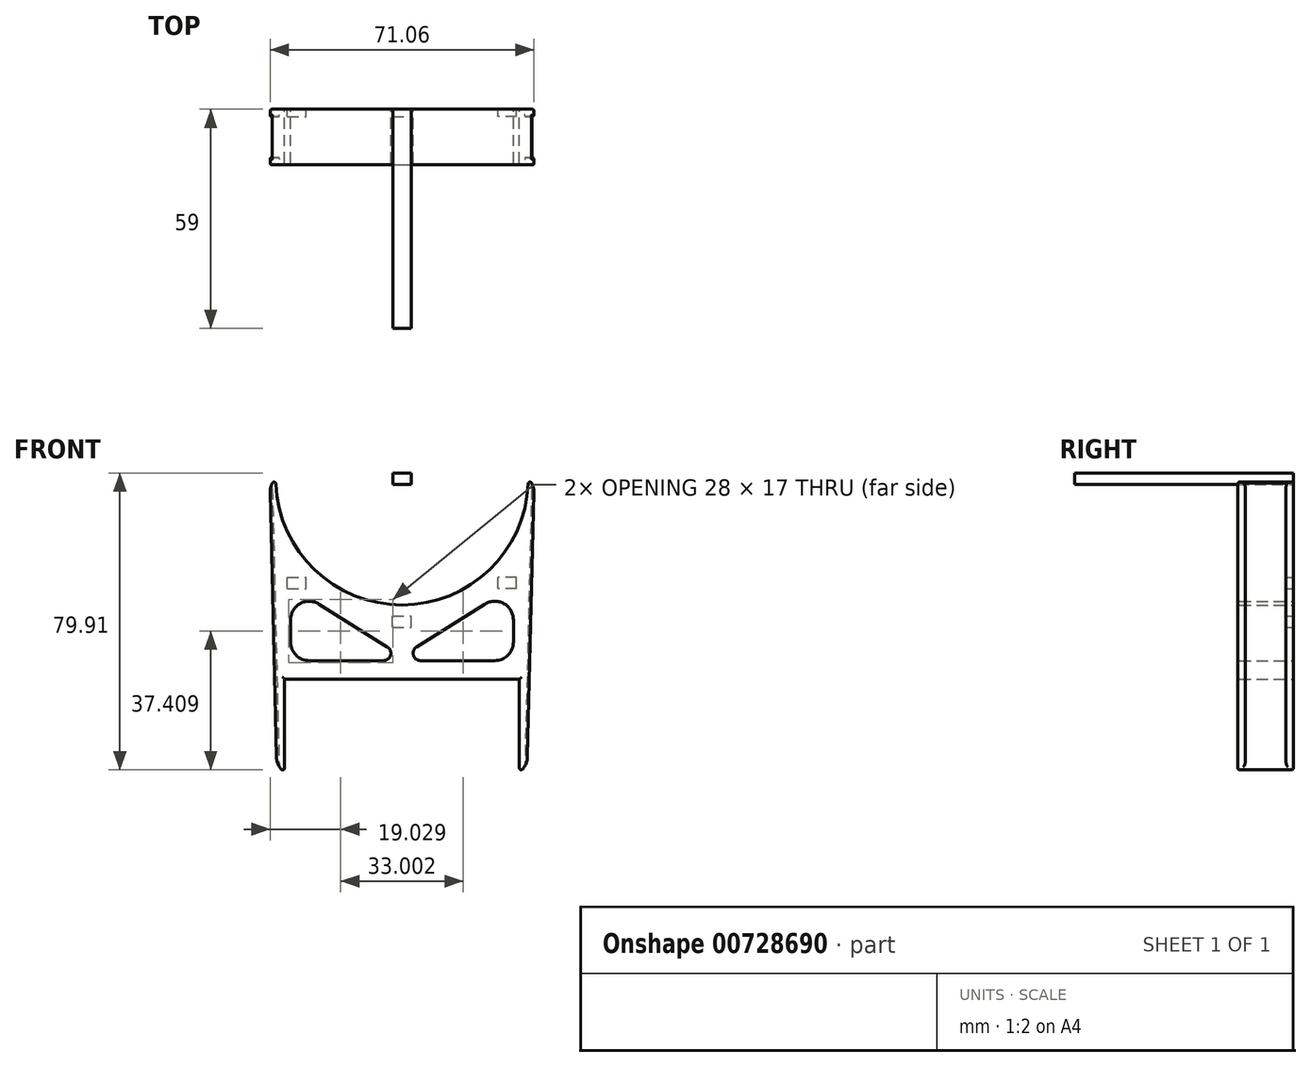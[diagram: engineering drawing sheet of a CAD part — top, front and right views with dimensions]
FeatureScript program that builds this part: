
annotation { "Feature Type Name" : "Feature", "Feature Type Description" : "" }
export const myFeature = defineFeature(function(context is Context, id is Id, definition is map)
    precondition{}
    {
        {
            var Q0;
            Q0=qCreatedBy(makeId("Front.planeOp"),FACE);
            var sketch = newSketch(context, id + "F0", { "sketchPlane" : qUnion([Q0])});
            skArc(sketch, "E0", {"start": v(-34, 0) * mm, "mid": v(0, -34) * mm, "end": v(34, 0) * mm});
            skLineSegment(sketch, "E1", {"start": v(-31.62, -54) * mm, "end": v(31.63, -54) * mm});
            skLineSegment(sketch, "E2", {"start": v(31.63, -54) * mm, "end": v(31.63, -79) * mm});
            skLineSegment(sketch, "E3", {"start": v(33.8, -75) * mm, "end": v(35.53, -3.72) * mm});
            skArc(sketch, "E4", {"start": v(33.8, -75) * mm, "mid": v(33.2, -77.26) * mm, "end": v(31.63, -79) * mm});
            skArc(sketch, "E5.MirrorCS", {"start": v(-33.8, -75) * mm, "mid": v(-33.2, -77.26) * mm, "end": v(-31.63, -79) * mm});
            skLineSegment(sketch, "E6", {"start": v(-31.62, -54) * mm, "end": v(-31.63, -79) * mm});
            skLineSegment(sketch, "E7", {"start": v(-30, -44) * mm, "end": v(-30, -38) * mm});
            skLineSegment(sketch, "E8", {"start": v(-25, -49) * mm, "end": v(-5, -49) * mm});
            skLineSegment(sketch, "E9", {"start": v(-3.94, -45.3) * mm, "end": v(-22.34, -33.76) * mm});
            skPoint(sketch, "E10.visualSharp", {"position": v(-30, -28.96) * mm});
            skArc(sketch, "E10.filletArc", {"start": v(-22.34, -33.76) * mm, "mid": v(-27.42, -33.63) * mm, "end": v(-30, -38) * mm});
            skPoint(sketch, "E11.visualSharp", {"position": v(1.95, -49) * mm});
            skArc(sketch, "E11.filletArc", {"start": v(-5, -49) * mm, "mid": v(-3.08, -47.55) * mm, "end": v(-3.94, -45.3) * mm});
            skPoint(sketch, "E12.visualSharp", {"position": v(-30, -49) * mm});
            skArc(sketch, "E12.filletArc", {"start": v(-30, -44) * mm, "mid": v(-28.54, -47.54) * mm, "end": v(-25, -49) * mm});
            skArc(sketch, "E13.MirrorCS", {"start": v(22.34, -33.76) * mm, "mid": v(27.42, -33.63) * mm, "end": v(30, -38) * mm});
            skLineSegment(sketch, "E14.MirrorCS", {"start": v(3.94, -45.3) * mm, "end": v(22.34, -33.76) * mm});
            skLineSegment(sketch, "E15.MirrorCS", {"start": v(25, -49) * mm, "end": v(5, -49) * mm});
            skArc(sketch, "E16.MirrorCS", {"start": v(30, -44) * mm, "mid": v(28.54, -47.54) * mm, "end": v(25, -49) * mm});
            skLineSegment(sketch, "E17.MirrorCS", {"start": v(30, -44) * mm, "end": v(30, -38) * mm});
            skArc(sketch, "E18.MirrorCS", {"start": v(5, -49) * mm, "mid": v(3.08, -47.55) * mm, "end": v(3.94, -45.3) * mm});
            skArc(sketch, "E19", {"start": v(35.53, -3.72) * mm, "mid": v(35.16, -1.7) * mm, "end": v(34, 0) * mm});
            skArc(sketch, "E20.MirrorCS", {"start": v(-35.53, -3.72) * mm, "mid": v(-35.16, -1.7) * mm, "end": v(-34, 0) * mm});
            skLineSegment(sketch, "E21.MirrorCS", {"start": v(-33.8, -75) * mm, "end": v(-35.53, -3.72) * mm});
            skSolve(sketch);
        }
        {
            var Q0;
            Q0 = qSketchRegion(id + "F0", true);
            extrude(context, id + "F1", {"entities" : qUnion([Q0]), "depth" : 15 * mm, "offsetDistance" : 25 * mm});
        }
        {
            var Q0;
            Q0=qCreatedBy(makeId("Front.planeOp"),FACE);
            cPlane(context, id + "F2", {"entities" : qUnion([Q0]), "cplaneType" : CPlaneType.OFFSET, "offset" : 2 * mm, "width" : 150 * mm, "height" : 150 * mm});
        }
        {
            var Q0;
            Q0=qCreatedBy(id+"F2.planeOp",FACE);
            var sketch = newSketch(context, id + "F3", { "sketchPlane" : qUnion([Q0])});
            skLineSegment(sketch, "E22.0", {"start": v(33.8, -75) * mm, "end": v(33.8, -75) * mm});
            skArc(sketch, "E23.0", {"start": v(33.8, -75) * mm, "mid": v(33.6, -76.25) * mm, "end": v(33.1, -77.4) * mm});
            skLineSegment(sketch, "E24.MirrorCS", {"start": v(-33.8, -75) * mm, "end": v(-33.8, -75) * mm});
            skLineSegment(sketch, "E25.0", {"start": v(33.8, -75) * mm, "end": v(35.53, -3.72) * mm});
            skArc(sketch, "E26.0", {"start": v(35.53, -3.72) * mm, "mid": v(35.4, -2.47) * mm, "end": v(34.96, -1.28) * mm});
            skLineSegment(sketch, "E27", {"start": v(34.96, -1.28) * mm, "end": v(33.1, -77.4) * mm});
            skPoint(sketch, "E28.orphan", {"position": v(34, 0) * mm});
            skLineSegment(sketch, "E29.MirrorCS", {"start": v(-34.96, -1.28) * mm, "end": v(-33.1, -77.4) * mm});
            skArc(sketch, "E30.MirrorCS", {"start": v(-35.53, -3.72) * mm, "mid": v(-35.4, -2.47) * mm, "end": v(-34.96, -1.28) * mm});
            skLineSegment(sketch, "E31.MirrorCS", {"start": v(-33.8, -75) * mm, "end": v(-35.53, -3.72) * mm});
            skArc(sketch, "E32.MirrorCS", {"start": v(-33.8, -75) * mm, "mid": v(-33.6, -76.25) * mm, "end": v(-33.1, -77.4) * mm});
            skSolve(sketch);
        }
        {
            var Q0;
            Q0 = qSketchRegion(id + "F3", true);
            extrude(context, id + "F4", {"entities" : qUnion([Q0]), "operationType" : NewBodyOperationType.REMOVE, "depth" : 11 * mm, "offsetDistance" : 25 * mm});
        }
        {
            var Q0;
            Q0=makeQuery(id+"F1.opExtrude","CAP_FACE",FACE,{"disambiguationData":[OSD([sQuery(id+"F0.wireOp",EDGE,"E0"),sQuery(id+"F0.wireOp",EDGE,"E1"),sQuery(id+"F0.wireOp",EDGE,"E2"),sQuery(id+"F0.wireOp",EDGE,"E3"),sQuery(id+"F0.wireOp",EDGE,"E4"),sQuery(id+"F0.wireOp",EDGE,"E5.MirrorCS"),sQuery(id+"F0.wireOp",EDGE,"E6"),sQuery(id+"F0.wireOp",EDGE,"E7"),sQuery(id+"F0.wireOp",EDGE,"E8"),sQuery(id+"F0.wireOp",EDGE,"E9"),sQuery(id+"F0.wireOp",EDGE,"E10.filletArc"),sQuery(id+"F0.wireOp",EDGE,"E11.filletArc"),sQuery(id+"F0.wireOp",EDGE,"E12.filletArc"),sQuery(id+"F0.wireOp",EDGE,"E13.MirrorCS"),sQuery(id+"F0.wireOp",EDGE,"E14.MirrorCS"),sQuery(id+"F0.wireOp",EDGE,"E15.MirrorCS"),sQuery(id+"F0.wireOp",EDGE,"E16.MirrorCS"),sQuery(id+"F0.wireOp",EDGE,"E17.MirrorCS"),sQuery(id+"F0.wireOp",EDGE,"E18.MirrorCS"),sQuery(id+"F0.wireOp",EDGE,"E19"),sQuery(id+"F0.wireOp",EDGE,"E20.MirrorCS"),sQuery(id+"F0.wireOp",EDGE,"E21.MirrorCS")])],"isStart":false});
            var Q1;
            Q1=makeQuery(id+"F1.opExtrude","CAP_FACE",FACE,{"disambiguationData":[OSD([sQuery(id+"F0.wireOp",EDGE,"E0"),sQuery(id+"F0.wireOp",EDGE,"E1"),sQuery(id+"F0.wireOp",EDGE,"E2"),sQuery(id+"F0.wireOp",EDGE,"E3"),sQuery(id+"F0.wireOp",EDGE,"E4"),sQuery(id+"F0.wireOp",EDGE,"E5.MirrorCS"),sQuery(id+"F0.wireOp",EDGE,"E6"),sQuery(id+"F0.wireOp",EDGE,"E7"),sQuery(id+"F0.wireOp",EDGE,"E8"),sQuery(id+"F0.wireOp",EDGE,"E9"),sQuery(id+"F0.wireOp",EDGE,"E10.filletArc"),sQuery(id+"F0.wireOp",EDGE,"E11.filletArc"),sQuery(id+"F0.wireOp",EDGE,"E12.filletArc"),sQuery(id+"F0.wireOp",EDGE,"E13.MirrorCS"),sQuery(id+"F0.wireOp",EDGE,"E14.MirrorCS"),sQuery(id+"F0.wireOp",EDGE,"E15.MirrorCS"),sQuery(id+"F0.wireOp",EDGE,"E16.MirrorCS"),sQuery(id+"F0.wireOp",EDGE,"E17.MirrorCS"),sQuery(id+"F0.wireOp",EDGE,"E18.MirrorCS"),sQuery(id+"F0.wireOp",EDGE,"E19"),sQuery(id+"F0.wireOp",EDGE,"E20.MirrorCS"),sQuery(id+"F0.wireOp",EDGE,"E21.MirrorCS")])],"isStart":true});
            var Q2;
            {var subQ0=sQuery(id+"F0.wireOp",EDGE,"E21.MirrorCS");Q2=makeQuery(id+"F4.boolean.opBoolean","SPLIT",FACE,{"disambiguationData":[TD([makeQuery(id+"F4.opExtrude","CAP_FACE",FACE,{"disambiguationData":[OSD([sQuery(id+"F3.wireOp",EDGE,"E29.MirrorCS"),sQuery(id+"F3.wireOp",EDGE,"E30.MirrorCS"),sQuery(id+"F3.wireOp",EDGE,"E31.MirrorCS"),sQuery(id+"F3.wireOp",EDGE,"E32.MirrorCS")])],"isStart":false})])],"derivedFrom":makeQuery(id+"F1.opExtrude","SWEPT_FACE",FACE,{"disambiguationData":[OSD([subQ0])]})});}
            var Q3;
            {var subQ0=sQuery(id+"F0.wireOp",EDGE,"E21.MirrorCS");Q3=makeQuery(id+"F4.boolean.opBoolean","SPLIT",FACE,{"disambiguationData":[TD([makeQuery(id+"F4.opExtrude","CAP_FACE",FACE,{"disambiguationData":[OSD([sQuery(id+"F3.wireOp",EDGE,"E29.MirrorCS"),sQuery(id+"F3.wireOp",EDGE,"E30.MirrorCS"),sQuery(id+"F3.wireOp",EDGE,"E31.MirrorCS"),sQuery(id+"F3.wireOp",EDGE,"E32.MirrorCS")])],"isStart":true})])],"derivedFrom":makeQuery(id+"F1.opExtrude","SWEPT_FACE",FACE,{"disambiguationData":[OSD([subQ0])]})});}
            var Q4;
            Q4=makeQuery(id+"F1.opExtrude","SWEPT_FACE",FACE,{"disambiguationData":[OSD([sQuery(id+"F0.wireOp",EDGE,"E20.MirrorCS")])]});
            var Q5;
            Q5=makeQuery(id+"F1.opExtrude","SWEPT_FACE",FACE,{"disambiguationData":[OSD([sQuery(id+"F0.wireOp",EDGE,"E5.MirrorCS")])]});
            var Q6;
            Q6=makeQuery(id+"F1.opExtrude","SWEPT_FACE",FACE,{"disambiguationData":[OSD([sQuery(id+"F0.wireOp",EDGE,"E19")])]});
            var Q7;
            {var subQ2=sQuery(id+"F0.wireOp",EDGE,"E3");Q7=makeQuery(id+"F4.boolean.opBoolean","SPLIT",FACE,{"disambiguationData":[TD([makeQuery(id+"F4.opExtrude","CAP_FACE",FACE,{"disambiguationData":[OSD([sQuery(id+"F3.wireOp",EDGE,"E23.0"),sQuery(id+"F3.wireOp",EDGE,"E25.0"),sQuery(id+"F3.wireOp",EDGE,"E26.0"),sQuery(id+"F3.wireOp",EDGE,"E27")])],"isStart":false})])],"derivedFrom":makeQuery(id+"F1.opExtrude","SWEPT_FACE",FACE,{"disambiguationData":[OSD([subQ2])]})});}
            var Q8;
            {var subQ2=sQuery(id+"F0.wireOp",EDGE,"E3");Q8=makeQuery(id+"F4.boolean.opBoolean","SPLIT",FACE,{"disambiguationData":[TD([makeQuery(id+"F4.opExtrude","CAP_FACE",FACE,{"disambiguationData":[OSD([sQuery(id+"F3.wireOp",EDGE,"E23.0"),sQuery(id+"F3.wireOp",EDGE,"E25.0"),sQuery(id+"F3.wireOp",EDGE,"E26.0"),sQuery(id+"F3.wireOp",EDGE,"E27")])],"isStart":true})])],"derivedFrom":makeQuery(id+"F1.opExtrude","SWEPT_FACE",FACE,{"disambiguationData":[OSD([subQ2])]})});}
            var Q9;
            Q9=makeQuery(id+"F1.opExtrude","SWEPT_FACE",FACE,{"disambiguationData":[OSD([sQuery(id+"F0.wireOp",EDGE,"E4")])]});
            fillet(context, id + "F5", {"entities" : qUnion([Q0, Q1, Q2, Q3, Q4, Q5, Q6, Q7, Q8, Q9]), "radius" : 0.5 * mm, "tangentPropagation" : true, "allowEdgeOverflow" : false});
        }
        {
            var Q0;
            Q0=qCreatedBy(makeId("Front.planeOp"),FACE);
            var sketch = newSketch(context, id + "F6", { "sketchPlane" : qUnion([Q0])});
            skLineSegment(sketch, "E33.bottom", {"start": v(-2.52, -40.03) * mm, "end": v(2.52, -40.03) * mm});
            skLineSegment(sketch, "E33.top", {"start": v(-2.52, -36.98) * mm, "end": v(2.52, -36.98) * mm});
            skLineSegment(sketch, "E33.left", {"start": v(-2.52, -40.03) * mm, "end": v(-2.52, -36.98) * mm});
            skLineSegment(sketch, "E33.right", {"start": v(2.52, -40.03) * mm, "end": v(2.52, -36.98) * mm});
            skPoint(sketch, "E33.middle", {"position": v(0, -38.5) * mm});
            skLineSegment(sketch, "E34.bottom", {"start": v(-30.86, -29.62) * mm, "end": v(-25.8, -29.62) * mm});
            skLineSegment(sketch, "E34.top", {"start": v(-30.86, -26.57) * mm, "end": v(-25.8, -26.57) * mm});
            skLineSegment(sketch, "E34.left", {"start": v(-30.86, -29.62) * mm, "end": v(-30.86, -26.57) * mm});
            skLineSegment(sketch, "E34.right", {"start": v(-25.8, -29.62) * mm, "end": v(-25.8, -26.57) * mm});
            skLineSegment(sketch, "E35.MirrorCS", {"start": v(30.86, -26.57) * mm, "end": v(25.8, -26.57) * mm});
            skLineSegment(sketch, "E36.MirrorCS", {"start": v(30.86, -29.62) * mm, "end": v(30.86, -26.57) * mm});
            skLineSegment(sketch, "E37.MirrorCS", {"start": v(30.86, -29.62) * mm, "end": v(25.8, -29.62) * mm});
            skLineSegment(sketch, "E38.MirrorCS", {"start": v(25.8, -29.62) * mm, "end": v(25.8, -26.57) * mm});
            skSolve(sketch);
        }
        {
            var Q0;
            Q0 = qSketchRegion(id + "F6", true);
            extrude(context, id + "F7", {"entities" : qUnion([Q0]), "operationType" : NewBodyOperationType.REMOVE, "depth" : 2 * mm, "offsetDistance" : 25 * mm});
        }
        {
            var Q0;
            Q0=qCreatedBy(makeId("Front.planeOp"),FACE);
            var sketch = newSketch(context, id + "F8", { "sketchPlane" : qUnion([Q0])});
            skLineSegment(sketch, "E39.bottom", {"start": v(-2.5, -1.5) * mm, "end": v(2.5, -1.5) * mm});
            skLineSegment(sketch, "E39.top", {"start": v(-2.5, 1.5) * mm, "end": v(2.5, 1.5) * mm});
            skLineSegment(sketch, "E39.left", {"start": v(-2.5, -1.5) * mm, "end": v(-2.5, 1.5) * mm});
            skLineSegment(sketch, "E39.right", {"start": v(2.5, -1.5) * mm, "end": v(2.5, 1.5) * mm});
            skPoint(sketch, "E39.middle", {"position": v(0, 0) * mm});
            skSolve(sketch);
        }
        {
            var Q0;
            Q0 = qSketchRegion(id + "F8", true);
            extrude(context, id + "F9", {"entities" : qUnion([Q0]), "depth" : 59 * mm, "offsetDistance" : 25 * mm});
        }
    });
